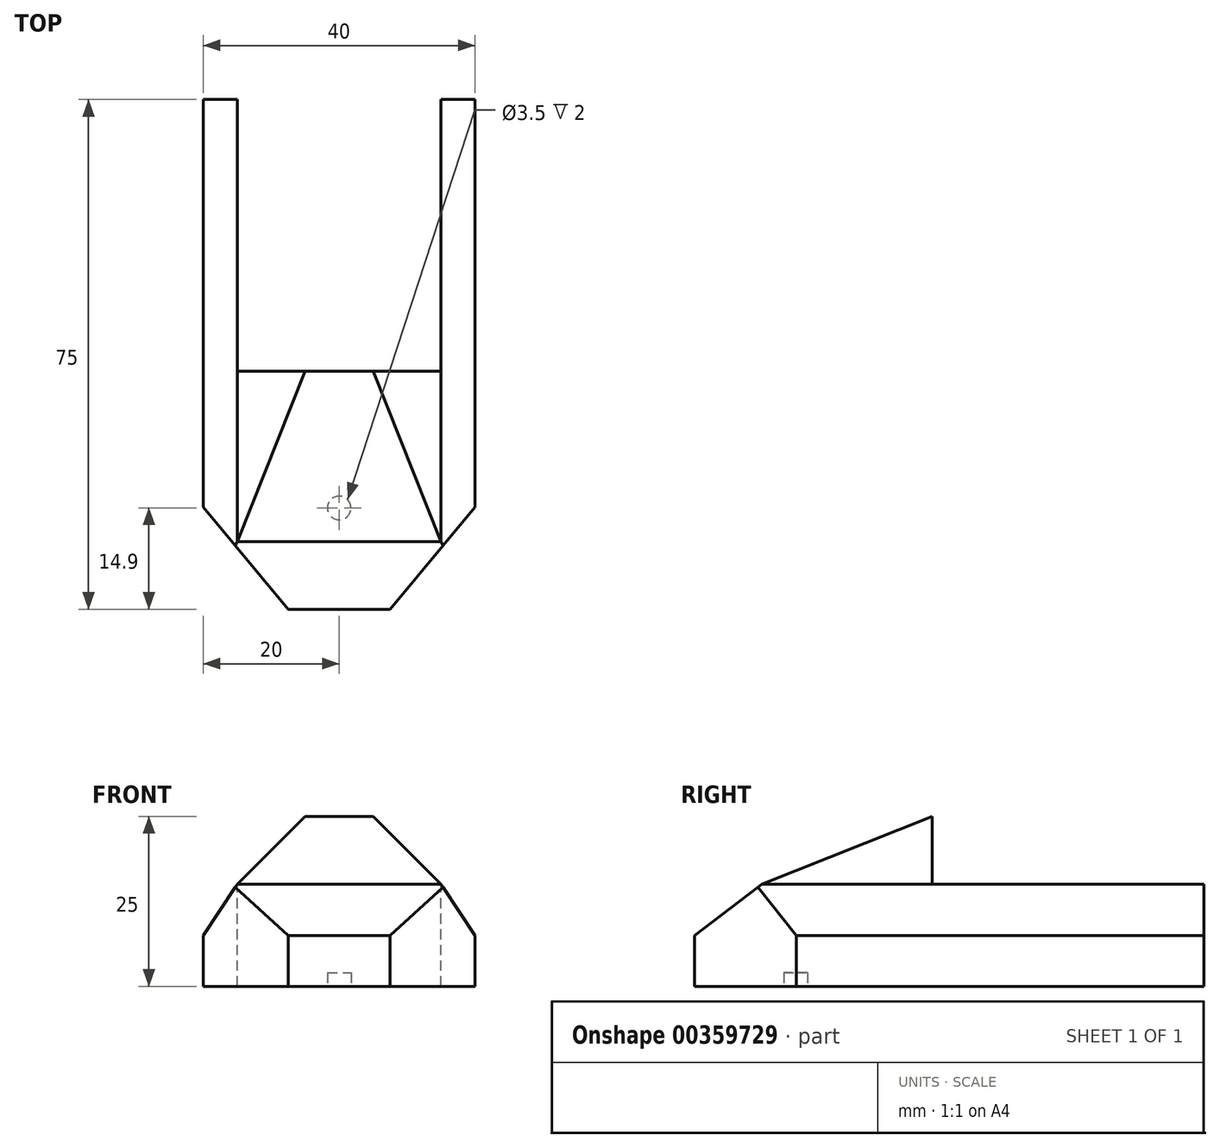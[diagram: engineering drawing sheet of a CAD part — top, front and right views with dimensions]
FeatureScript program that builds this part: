
annotation { "Feature Type Name" : "Feature", "Feature Type Description" : "" }
export const myFeature = defineFeature(function(context is Context, id is Id, definition is map)
    precondition{}
    {
        {
            var Q0;
            Q0=qCreatedBy(makeId("Right.planeOp"),FACE);
            var sketch = newSketch(context, id + "F0", { "sketchPlane" : qUnion([Q0])});
            skLineSegment(sketch, "E0.bottom", {"start": v(37.5, 17.5) * mm, "end": v(-37.5, 17.5) * mm});
            skLineSegment(sketch, "E0.top", {"start": v(37.5, -17.5) * mm, "end": v(-37.5, -17.5) * mm});
            skLineSegment(sketch, "E0.left", {"start": v(37.5, 17.5) * mm, "end": v(37.5, -17.5) * mm});
            skLineSegment(sketch, "E0.right", {"start": v(-37.5, 17.5) * mm, "end": v(-37.5, -17.5) * mm});
            skPoint(sketch, "E0.middle", {"position": v(0, 0) * mm});
            skLineSegment(sketch, "E1.bottom", {"start": v(37.5, 17.5) * mm, "end": v(-2.5, 17.5) * mm});
            skLineSegment(sketch, "E1.top", {"start": v(37.5, -2.5) * mm, "end": v(-2.5, -2.5) * mm});
            skLineSegment(sketch, "E1.left", {"start": v(37.5, 17.5) * mm, "end": v(37.5, -2.5) * mm});
            skLineSegment(sketch, "E1.right", {"start": v(-2.5, 17.5) * mm, "end": v(-2.5, -2.5) * mm});
            skLineSegment(sketch, "E2", {"start": v(37.5, -10) * mm, "end": v(-37.5, -10) * mm});
            skLineSegment(sketch, "E3", {"start": v(-2.5, -2.5) * mm, "end": v(-37.5, -2.5) * mm});
            skLineSegment(sketch, "E4", {"start": v(-37.5, -10) * mm, "end": v(-27.58, -2.5) * mm});
            skLineSegment(sketch, "E5", {"start": v(-27.58, -2.5) * mm, "end": v(-2.5, 7.5) * mm});
            skSolve(sketch);
        }
        {
            var Q0;
            {var subQ0=sQuery(id+"F0.wireOp",EDGE,"E0.top");Q0=makeQuery(id+"F0.imprint","IMPRINT",FACE,{"disambiguationData":[TD([[makeQuery(id+"F0.imprint","IMPRINT",EDGE,{"derivedFrom":subQ0}),-1.0]])]});}
            var Q1;
            {var subQ1=sQuery(id+"F0.wireOp",EDGE,"E1.top");Q1=makeQuery(id+"F0.imprint","IMPRINT",FACE,{"disambiguationData":[TD([[makeQuery(id+"F0.imprint","IMPRINT",EDGE,{"derivedFrom":subQ1}),1.0]])]});}
            var Q2;
            {var subQ3=sQuery(id+"F0.wireOp",EDGE,"E5");Q2=makeQuery(id+"F0.imprint","IMPRINT",FACE,{"disambiguationData":[TD([[makeQuery(id+"F0.imprint","IMPRINT",EDGE,{"derivedFrom":subQ3}),-1.0]])]});}
            extrude(context, id + "F1", {"entities" : qUnion([Q0, Q1, Q2]), "depth" : 40 * mm});
        }
        {
            var Q0;
            Q0=makeQuery(id+"F1.opExtrude","SWEPT_FACE",FACE,{"disambiguationData":[OSD([sQuery(id+"F0.wireOp",EDGE,"E1.top")])]});
            var sketch = newSketch(context, id + "F2", { "sketchPlane" : qUnion([Q0])});
            skLineSegment(sketch, "E6.bottom", {"start": v(5, 37.5) * mm, "end": v(35, 37.5) * mm});
            skLineSegment(sketch, "E6.top", {"start": v(5, -2.5) * mm, "end": v(35, -2.5) * mm});
            skLineSegment(sketch, "E6.left", {"start": v(5, 37.5) * mm, "end": v(5, -2.5) * mm});
            skLineSegment(sketch, "E6.right", {"start": v(35, 37.5) * mm, "end": v(35, -2.5) * mm});
            skSolve(sketch);
        }
        {
            var Q0;
            Q0 = qSketchRegion(id + "F2", true);
            extrude(context, id + "F3", {"entities" : qUnion([Q0]), "operationType" : NewBodyOperationType.REMOVE, "endBound" : BoundingType.THROUGH_ALL, "oppositeDirection" : true, "depth" : 25 * mm});
        }
        {
            var Q0;
            {var subQ2=sQuery(id+"F0.wireOp",EDGE,"E0.left");Q0=makeQuery(id+"F3.boolean.opBoolean","SPLIT",FACE,{"disambiguationData":[TD([makeQuery(id+"F3.opExtrude","SWEPT_FACE",FACE,{"disambiguationData":[OSD([sQuery(id+"F2.wireOp",EDGE,"E6.right")])]})])],"derivedFrom":makeQuery(id+"F1.opExtrude","SWEPT_FACE",FACE,{"disambiguationData":[OSD([subQ2])]})});}
            var sketch = newSketch(context, id + "F4", { "sketchPlane" : qUnion([Q0])});
            skLineSegment(sketch, "E7", {"start": v(-40, -10) * mm, "end": v(-35, -2.5) * mm});
            skSolve(sketch);
        }
        {
            var Q0;
            {var subQ2=sQuery(id+"F0.wireOp",EDGE,"E0.left");Q0=makeQuery(id+"F3.boolean.opBoolean","SPLIT",FACE,{"disambiguationData":[TD([makeQuery(id+"F3.opExtrude","SWEPT_FACE",FACE,{"disambiguationData":[OSD([sQuery(id+"F2.wireOp",EDGE,"E6.left")])]})])],"derivedFrom":makeQuery(id+"F1.opExtrude","SWEPT_FACE",FACE,{"disambiguationData":[OSD([subQ2])]})});}
            var sketch = newSketch(context, id + "F5", { "sketchPlane" : qUnion([Q0])});
            skLineSegment(sketch, "E8", {"start": v(0, -10) * mm, "end": v(-5, -2.5) * mm});
            skSolve(sketch);
        }
        {
            var Q0;
            Q0=makeQuery(id+"F3.boolean.opBoolean","MERGE",FACE,{"derivedFrom":[makeQuery(id+"F1.opExtrude","SWEPT_FACE",FACE,{"disambiguationData":[OSD([sQuery(id+"F0.wireOp",EDGE,"E1.right")])]}),makeQuery(id+"F3.opExtrude","SWEPT_FACE",FACE,{"disambiguationData":[OSD([sQuery(id+"F2.wireOp",EDGE,"E6.top")])]})]});
            var sketch = newSketch(context, id + "F6", { "sketchPlane" : qUnion([Q0])});
            skLineSegment(sketch, "E9", {"start": v(-35, -2.5) * mm, "end": v(-25, 7.5) * mm});
            skLineSegment(sketch, "E10", {"start": v(-5, -2.5) * mm, "end": v(-15, 7.5) * mm});
            skSolve(sketch);
        }
        {
            var Q0;
            {var subQ0=sQuery(id+"F6.wireOp",EDGE,"E9");Q0=makeQuery(id+"F6.imprint","IMPRINT",FACE,{"disambiguationData":[TD([[makeQuery(id+"F6.imprint","IMPRINT",EDGE,{"derivedFrom":subQ0}),1.0]])]});}
            var Q1;
            {var subQ0=sQuery(id+"F4.wireOp",EDGE,"E7");Q1=makeQuery(id+"F4.imprint","IMPRINT",FACE,{"disambiguationData":[TD([[makeQuery(id+"F4.imprint","IMPRINT",EDGE,{"derivedFrom":subQ0}),1.0]])]});}
            var Q2;
            {var subQ0=sQuery(id+"F6.wireOp",EDGE,"E10");Q2=makeQuery(id+"F6.imprint","IMPRINT",FACE,{"disambiguationData":[TD([[makeQuery(id+"F6.imprint","IMPRINT",EDGE,{"derivedFrom":subQ0}),-1.0]])]});}
            var Q3;
            {var subQ0=sQuery(id+"F5.wireOp",EDGE,"E8");Q3=makeQuery(id+"F5.imprint","IMPRINT",FACE,{"disambiguationData":[TD([[makeQuery(id+"F5.imprint","IMPRINT",EDGE,{"derivedFrom":subQ0}),-1.0]])]});}
            extrude(context, id + "F7", {"entities" : qUnion([Q0, Q1, Q2, Q3]), "operationType" : NewBodyOperationType.REMOVE, "endBound" : BoundingType.THROUGH_ALL, "oppositeDirection" : true, "depth" : 25 * mm});
        }
        {
            var Q0;
            Q0=makeQuery(id+"F1.opExtrude","SWEPT_FACE",FACE,{"disambiguationData":[OSD([sQuery(id+"F0.wireOp",EDGE,"E0.top")])]});
            var sketch = newSketch(context, id + "F8", { "sketchPlane" : qUnion([Q0])});
            skLineSegment(sketch, "E11", {"start": v(0, 22.5) * mm, "end": v(12.5, 37.5) * mm});
            skLineSegment(sketch, "E12", {"start": v(27.5, 37.5) * mm, "end": v(40, 22.5) * mm});
            skSolve(sketch);
        }
        {
            var Q0;
            {var subQ0=sQuery(id+"F8.wireOp",EDGE,"E11");Q0=makeQuery(id+"F8.imprint","IMPRINT",FACE,{"disambiguationData":[TD([[makeQuery(id+"F8.imprint","IMPRINT",EDGE,{"derivedFrom":subQ0}),1.0]])]});}
            var Q1;
            {var subQ0=sQuery(id+"F8.wireOp",EDGE,"E12");Q1=makeQuery(id+"F8.imprint","IMPRINT",FACE,{"disambiguationData":[TD([[makeQuery(id+"F8.imprint","IMPRINT",EDGE,{"derivedFrom":subQ0}),1.0]])]});}
            extrude(context, id + "F9", {"entities" : qUnion([Q0, Q1]), "operationType" : NewBodyOperationType.REMOVE, "endBound" : BoundingType.THROUGH_ALL, "oppositeDirection" : true, "depth" : 25 * mm});
        }
        {
            var Q0;
            Q0=makeQuery(id+"F1.opExtrude","SWEPT_FACE",FACE,{"disambiguationData":[OSD([sQuery(id+"F0.wireOp",EDGE,"E0.top")])]});
            var sketch = newSketch(context, id + "F10", { "sketchPlane" : qUnion([Q0])});
            skCircle(sketch, "E13", {"center": v(20, 22.6) * mm, "radius": 1.75 * mm});
            skSolve(sketch);
        }
        {
            var Q0;
            Q0=makeQuery(id+"F10.imprint","IMPRINT",FACE,{"disambiguationData":[TD([[makeQuery(id+"F10.imprint","IMPRINT",EDGE,{"derivedFrom":sQuery(id+"F10.wireOp",EDGE,"E13")}),1.0]])]});
            extrude(context, id + "F11", {"entities" : qUnion([Q0]), "operationType" : NewBodyOperationType.REMOVE, "oppositeDirection" : true, "depth" : 2 * mm});
        }
    });
